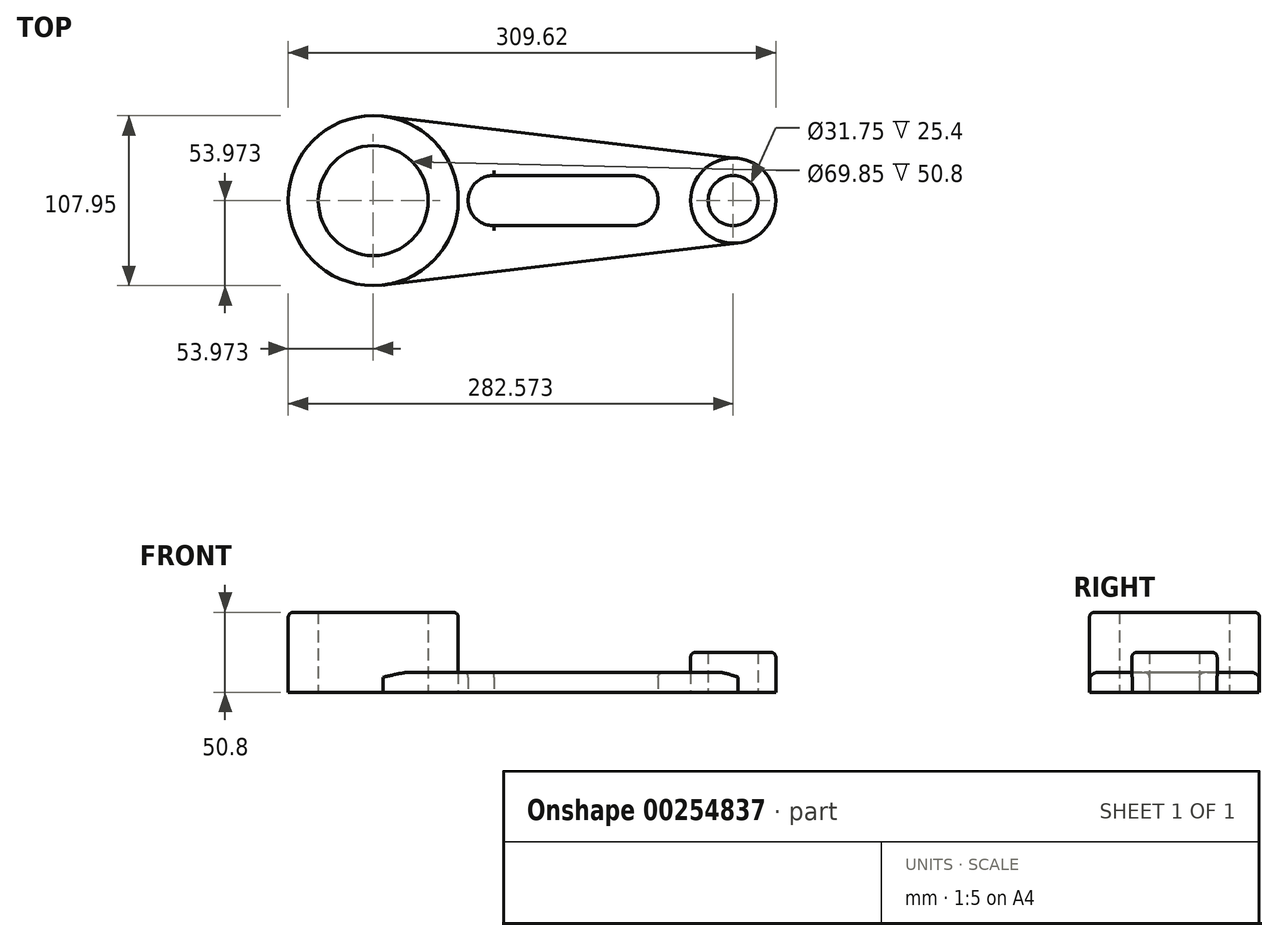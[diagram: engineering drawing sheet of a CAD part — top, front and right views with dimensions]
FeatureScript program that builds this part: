
annotation { "Feature Type Name" : "Feature", "Feature Type Description" : "" }
export const myFeature = defineFeature(function(context is Context, id is Id, definition is map)
    precondition{}
    {
        {
            var Q0;
            Q0=qCreatedBy(makeId("Top.planeOp"),FACE);
            var sketch = newSketch(context, id + "F0", { "sketchPlane" : qUnion([Q0])});
            skCircle(sketch, "E0", {"center": v(-162.62, 46.6) * mm, "radius": 53.98 * mm});
            skCircle(sketch, "E1", {"center": v(-162.62, 46.6) * mm, "radius": 34.93 * mm});
            skCircle(sketch, "E2", {"center": v(65.98, 46.6) * mm, "radius": 27.05 * mm});
            skCircle(sketch, "E3", {"center": v(65.98, 46.6) * mm, "radius": 12.7 * mm});
            skLineSegment(sketch, "E4", {"start": v(-156.26, -7) * mm, "end": v(69.17, 19.73) * mm});
            skLineSegment(sketch, "E5", {"start": v(-156.26, 100.2) * mm, "end": v(69.17, 73.46) * mm});
            skArc(sketch, "E6", {"start": v(-85.84, 62.46) * mm, "mid": v(-102.3, 46.63) * mm, "end": v(-85.9, 30.73) * mm});
            skArc(sketch, "E7", {"start": v(2.48, 30.7) * mm, "mid": v(18.36, 46.58) * mm, "end": v(2.48, 62.46) * mm});
            skLineSegment(sketch, "E8", {"start": v(-85.9, 30.73) * mm, "end": v(2.48, 30.7) * mm});
            skLineSegment(sketch, "E9", {"start": v(-85.84, 62.46) * mm, "end": v(2.48, 62.46) * mm});
            skPoint(sketch, "E10.end.orphan", {"position": v(-35.38, 30.72) * mm});
            skPoint(sketch, "E10.start.orphan", {"position": v(-35.38, 62.46) * mm});
            skSolve(sketch);
        }
        {
            var Q0;
            Q0=makeQuery(id+"F0.imprint","IMPRINT",FACE,{"disambiguationData":[TD([[makeQuery(id+"F0.imprint","IMPRINT",EDGE,{"derivedFrom":sQuery(id+"F0.wireOp",EDGE,"E1")}),-1.0]])]});
            extrude(context, id + "F1", {"entities" : qUnion([Q0]), "depth" : 50.8 * mm});
        }
        {
            var Q0;
            Q0=makeQuery(id+"F0.imprint","IMPRINT",FACE,{"disambiguationData":[TD([[makeQuery(id+"F0.imprint","IMPRINT",EDGE,{"derivedFrom":sQuery(id+"F0.wireOp",EDGE,"E3")}),-1.0]])]});
            extrude(context, id + "F2", {"entities" : qUnion([Q0]), "depth" : 25.4 * mm});
        }
        {
            var Q0;
            {var subQ0=sQuery(id+"F0.wireOp",EDGE,"E4");Q0=makeQuery(id+"F0.imprint","IMPRINT",FACE,{"disambiguationData":[TD([[makeQuery(id+"F0.imprint","IMPRINT",EDGE,{"derivedFrom":subQ0}),1.0]])]});}
            extrude(context, id + "F3", {"entities" : qUnion([Q0]), "depth" : 12.7 * mm});
        }
        {
            var Q0;
            Q0=makeQuery(id+"F3.opExtrude","CAP_EDGE",EDGE,{"disambiguationData":[OSD([sQuery(id+"F0.wireOp",EDGE,"E4")])],"isStart":false});
            fillet(context, id + "F4", {"entities" : qUnion([Q0]), "radius" : 3.17 * mm, "tangentPropagation" : true, "allowEdgeOverflow" : false});
        }
        {
            var Q0;
            Q0=makeQuery(id+"F3.opExtrude","CAP_EDGE",EDGE,{"disambiguationData":[OSD([sQuery(id+"F0.wireOp",EDGE,"E5")])],"isStart":false});
            var Q1;
            Q1=makeQuery(id+"F1.opExtrude","CAP_EDGE",EDGE,{"disambiguationData":[OSD([sQuery(id+"F0.wireOp",EDGE,"E0")])],"isStart":false});
            var Q2;
            Q2=makeQuery(id+"F2.opExtrude","CAP_EDGE",EDGE,{"disambiguationData":[OSD([sQuery(id+"F0.wireOp",EDGE,"E2")])],"isStart":false});
            fillet(context, id + "F5", {"entities" : qUnion([Q0, Q1, Q2]), "radius" : 3.17 * mm, "tangentPropagation" : true, "allowEdgeOverflow" : false});
        }
        {
            var Q0;
            Q0=makeQuery(id+"F3.opExtrude","CAP_EDGE",EDGE,{"disambiguationData":[OSD([sQuery(id+"F0.wireOp",EDGE,"E9")])],"isStart":false});
            var Q1;
            Q1=makeQuery(id+"F3.opExtrude","CAP_EDGE",EDGE,{"disambiguationData":[OSD([sQuery(id+"F0.wireOp",EDGE,"E8")])],"isStart":false});
            var Q2;
            Q2=makeQuery(id+"F3.opExtrude","CAP_EDGE",EDGE,{"disambiguationData":[OSD([sQuery(id+"F0.wireOp",EDGE,"E6")])],"isStart":false});
            var Q3;
            Q3=makeQuery(id+"F3.opExtrude","CAP_EDGE",EDGE,{"disambiguationData":[OSD([sQuery(id+"F0.wireOp",EDGE,"E7")])],"isStart":false});
            fillet(context, id + "F6", {"entities" : qUnion([Q0, Q1, Q2, Q3]), "radius" : 3.17 * mm, "tangentPropagation" : true, "allowEdgeOverflow" : false});
        }
        {
            var Q0;
            Q0=sQuery(id+"F0.wireOp",VERTEX,"E0.center");
            var Q1;
            Q1=sQuery(id+"F0.wireOp",VERTEX,"E2.center");
            var Q2;
            Q2=makeQuery(id+"F2.opExtrude","SWEPT_BODY",BODY,{"disambiguationData":[OSD([sQuery(id+"F0.wireOp",EDGE,"E2"),sQuery(id+"F0.wireOp",EDGE,"E3")])]});
            hole(context, id + "F7", {"style" : HoleStyle.SIMPLE, "endStyle" : HoleEndStyle.THROUGH, "oppositeDirection" : true, "holeDiameter" : 31.75 * mm, "tappedDepth" : 12.7 * mm, "tapClearance" : 3, "locations" : qUnion([Q0, Q1]), "scope" : qUnion([Q2])});
        }
    });
